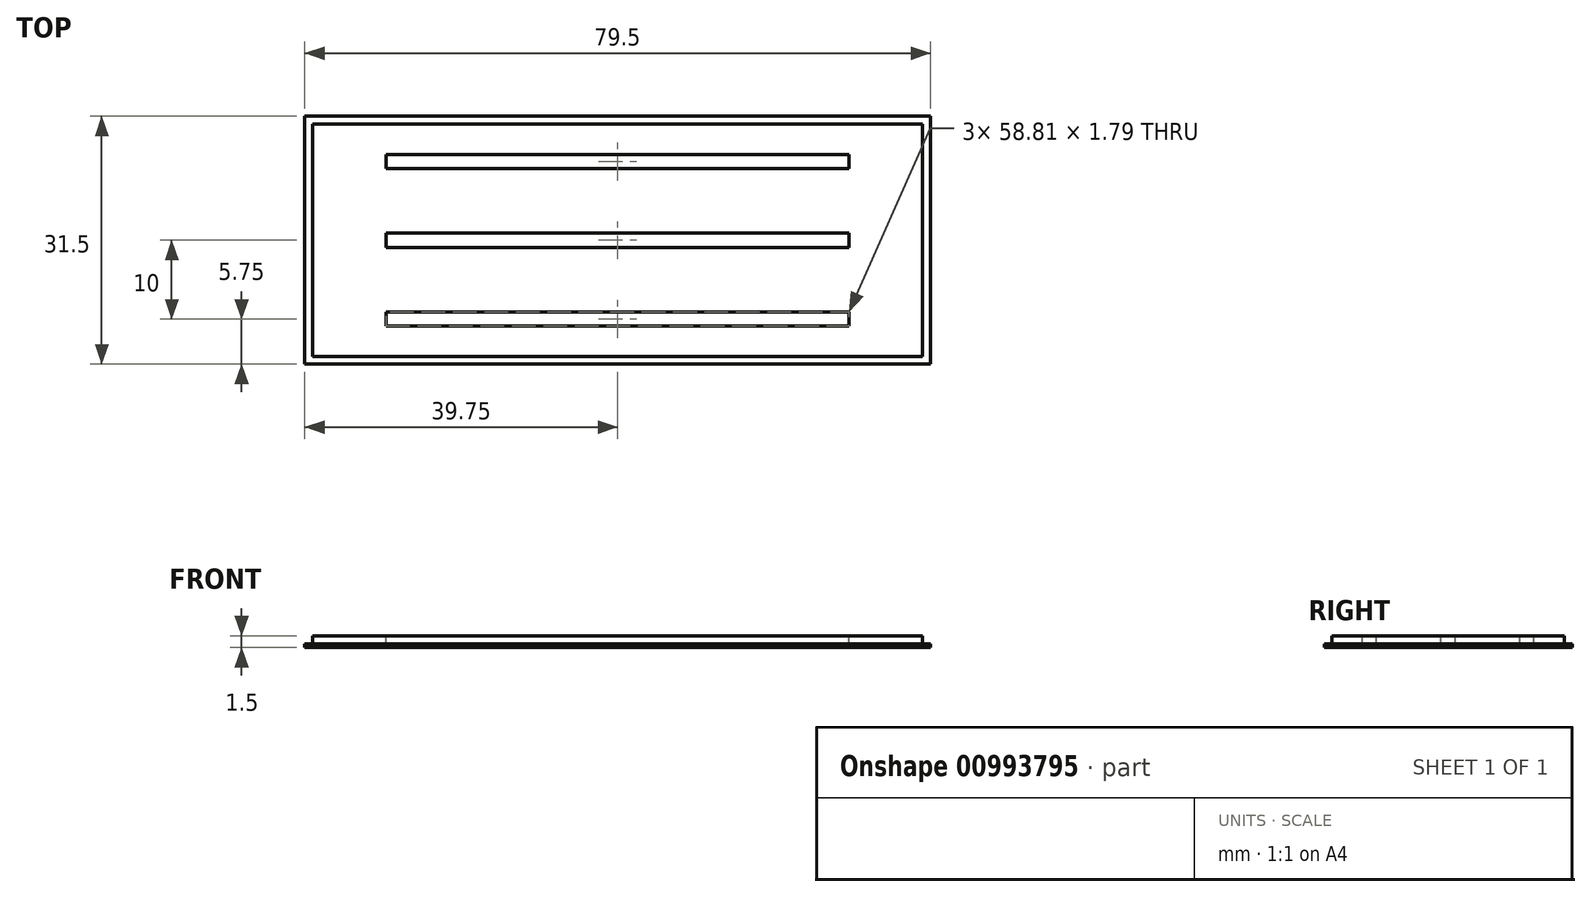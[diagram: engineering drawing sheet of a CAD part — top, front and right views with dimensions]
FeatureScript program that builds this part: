
annotation { "Feature Type Name" : "Feature", "Feature Type Description" : "" }
export const myFeature = defineFeature(function(context is Context, id is Id, definition is map)
    precondition{}
    {
        {
            var Q0;
            Q0=qCreatedBy(makeId("Top.planeOp"),FACE);
            var sketch = newSketch(context, id + "F0", { "sketchPlane" : qUnion([Q0])});
            skLineSegment(sketch, "E0.bottom", {"start": v(38.75, 14.75) * mm, "end": v(-38.75, 14.75) * mm});
            skLineSegment(sketch, "E0.top", {"start": v(38.75, -14.75) * mm, "end": v(-38.75, -14.75) * mm});
            skLineSegment(sketch, "E0.left", {"start": v(38.75, 14.75) * mm, "end": v(38.75, -14.75) * mm});
            skLineSegment(sketch, "E0.right", {"start": v(-38.75, 14.75) * mm, "end": v(-38.75, -14.75) * mm});
            skPoint(sketch, "E0.middle", {"position": v(0, 0) * mm});
            skLineSegment(sketch, "E1.bottom", {"start": v(39.75, 15.75) * mm, "end": v(-39.75, 15.75) * mm});
            skLineSegment(sketch, "E1.top", {"start": v(39.75, -15.75) * mm, "end": v(-39.75, -15.75) * mm});
            skLineSegment(sketch, "E1.left", {"start": v(39.75, 15.75) * mm, "end": v(39.75, -15.75) * mm});
            skLineSegment(sketch, "E1.right", {"start": v(-39.75, 15.75) * mm, "end": v(-39.75, -15.75) * mm});
            skLineSegment(sketch, "E2.bottom", {"start": v(29.4, 0.9) * mm, "end": v(-29.4, 0.9) * mm});
            skLineSegment(sketch, "E2.top", {"start": v(29.4, -0.9) * mm, "end": v(-29.4, -0.9) * mm});
            skLineSegment(sketch, "E2.left", {"start": v(29.4, 0.9) * mm, "end": v(29.4, -0.9) * mm});
            skLineSegment(sketch, "E2.right", {"start": v(-29.4, 0.9) * mm, "end": v(-29.4, -0.9) * mm});
            skLineSegment(sketch, "E3.0.1.0", {"start": v(29.4, -9.1) * mm, "end": v(-29.4, -9.1) * mm});
            skLineSegment(sketch, "E3.0.1.1", {"start": v(29.4, -10.9) * mm, "end": v(-29.4, -10.9) * mm});
            skLineSegment(sketch, "E3.0.1.2", {"start": v(29.4, -9.1) * mm, "end": v(29.4, -10.9) * mm});
            skLineSegment(sketch, "E3.0.1.3", {"start": v(-29.4, -9.1) * mm, "end": v(-29.4, -10.9) * mm});
            skLineSegment(sketch, "E3.direction1", {"start": v(-29.4, -0.9) * mm, "end": v(-4.4, -0.9) * mm, "construction": true});
            skLineSegment(sketch, "E3.direction2", {"start": v(-29.4, -0.9) * mm, "end": v(-29.4, -10.9) * mm, "construction": true});
            skLineSegment(sketch, "E4.0.1.0", {"start": v(-29.4, 10.9) * mm, "end": v(-29.4, 9.1) * mm});
            skLineSegment(sketch, "E4.0.1.1", {"start": v(29.4, 9.1) * mm, "end": v(-29.4, 9.1) * mm});
            skLineSegment(sketch, "E4.0.1.2", {"start": v(29.4, 10.9) * mm, "end": v(-29.4, 10.9) * mm});
            skLineSegment(sketch, "E4.0.1.3", {"start": v(29.4, 10.9) * mm, "end": v(29.4, 9.1) * mm});
            skLineSegment(sketch, "E4.direction2", {"start": v(-29.4, -0.9) * mm, "end": v(-29.4, 9.1) * mm, "construction": true});
            skSolve(sketch);
        }
        {
            var Q0;
            Q0=makeQuery(id+"F0.imprint","IMPRINT",FACE,{"disambiguationData":[TD([[makeQuery(id+"F0.imprint","IMPRINT",EDGE,{"derivedFrom":sQuery(id+"F0.wireOp",EDGE,"E0.bottom")}),-1.0]])]});
            var Q1;
            Q1=makeQuery(id+"F0.imprint","IMPRINT",FACE,{"disambiguationData":[TD([[makeQuery(id+"F0.imprint","IMPRINT",EDGE,{"derivedFrom":sQuery(id+"F0.wireOp",EDGE,"E0.bottom")}),1.0]])]});
            extrude(context, id + "F1", {"entities" : qUnion([Q0, Q1]), "oppositeDirection" : true, "depth" : 0.5 * mm, "offsetDistance" : 25 * mm});
        }
        {
            var Q0;
            Q0=makeQuery(id+"F0.imprint","IMPRINT",FACE,{"disambiguationData":[TD([[makeQuery(id+"F0.imprint","IMPRINT",EDGE,{"derivedFrom":sQuery(id+"F0.wireOp",EDGE,"E0.bottom")}),1.0]])]});
            extrude(context, id + "F2", {"entities" : qUnion([Q0]), "operationType" : NewBodyOperationType.ADD, "depth" : 1 * mm, "offsetDistance" : 25 * mm});
        }
    });
